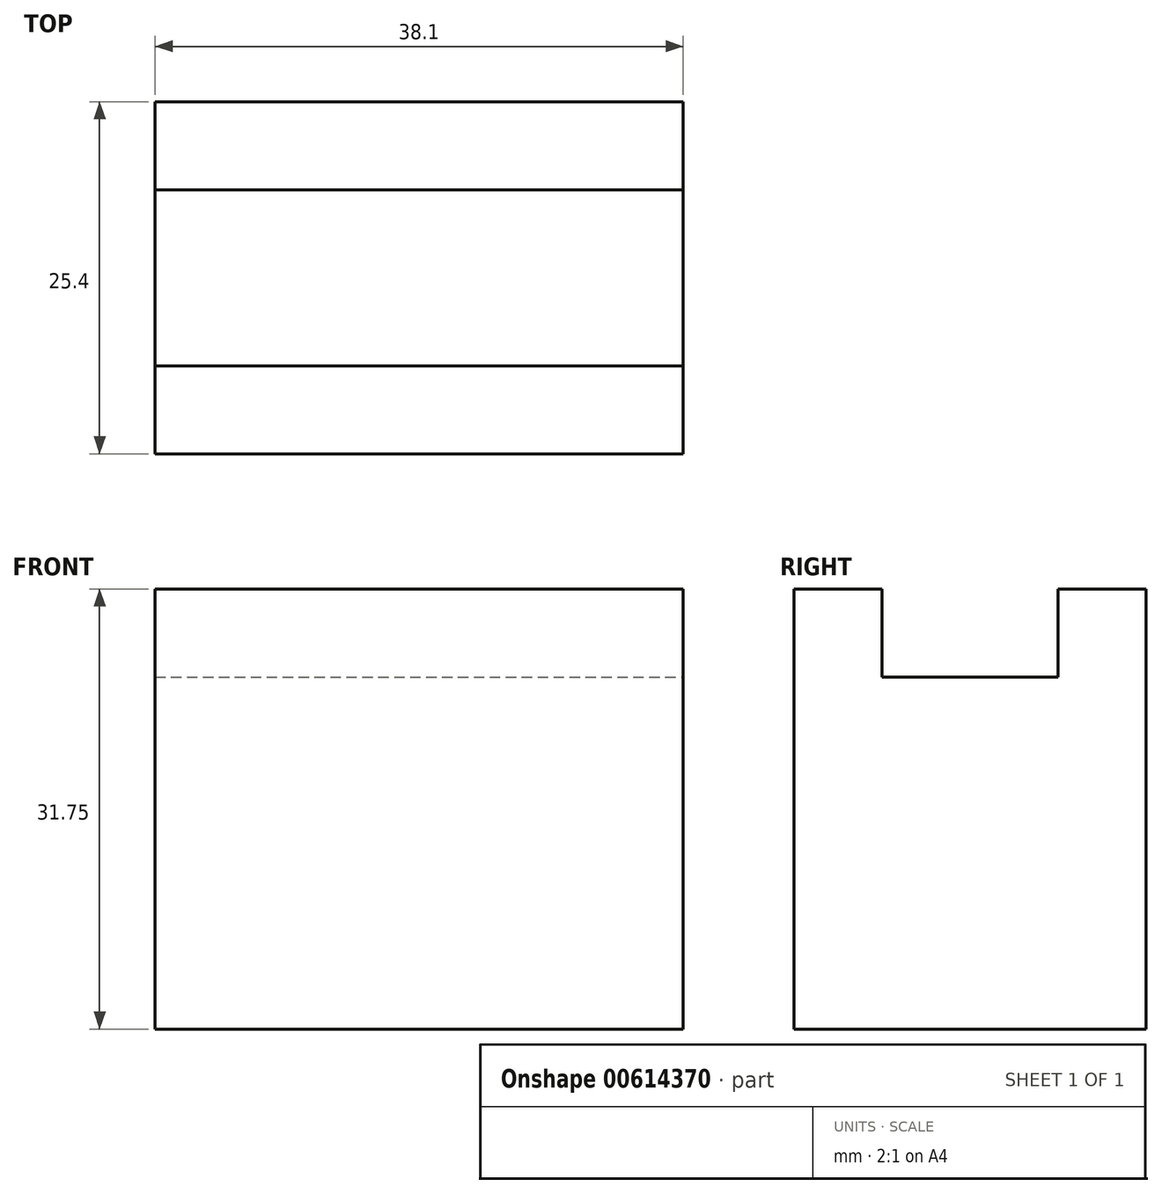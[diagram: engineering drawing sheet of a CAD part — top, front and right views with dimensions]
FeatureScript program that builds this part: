
annotation { "Feature Type Name" : "Feature", "Feature Type Description" : "" }
export const myFeature = defineFeature(function(context is Context, id is Id, definition is map)
    precondition{}
    {
        {
            var Q0;
            Q0=qCreatedBy(makeId("Front.planeOp"),FACE);
            var sketch = newSketch(context, id + "F0", { "sketchPlane" : qUnion([Q0])});
            skLineSegment(sketch, "E0", {"start": v(0, 0) * mm, "end": v(38.1, 0) * mm});
            skLineSegment(sketch, "E1", {"start": v(38.1, 0) * mm, "end": v(38.1, 31.75) * mm});
            skLineSegment(sketch, "E2", {"start": v(0, 0) * mm, "end": v(0, 31.75) * mm});
            skLineSegment(sketch, "E3", {"start": v(0, 31.75) * mm, "end": v(38.1, 31.75) * mm});
            skSolve(sketch);
        }
        {
            var Q0;
            Q0 = qSketchRegion(id + "F0", true);
            extrude(context, id + "F1", {"entities" : qUnion([Q0]), "depth" : 25.4 * mm, "offsetDistance" : 25.4 * mm});
        }
        {
            var Q0;
            Q0=makeQuery(id+"F1.opExtrude","SWEPT_FACE",FACE,{"disambiguationData":[OSD([sQuery(id+"F0.wireOp",EDGE,"E3")])]});
            var sketch = newSketch(context, id + "F2", { "sketchPlane" : qUnion([Q0])});
            skLineSegment(sketch, "E4", {"start": v(0, 0) * mm, "end": v(0, -6.35) * mm});
            skLineSegment(sketch, "E5", {"start": v(0, -25.4) * mm, "end": v(0, -19.05) * mm});
            skLineSegment(sketch, "E6", {"start": v(0, -19.05) * mm, "end": v(38.1, -19.05) * mm});
            skLineSegment(sketch, "E7", {"start": v(0, -6.35) * mm, "end": v(38.1, -6.35) * mm});
            skLineSegment(sketch, "E8", {"start": v(0, -6.35) * mm, "end": v(0, -19.05) * mm});
            skLineSegment(sketch, "E9", {"start": v(38.1, -6.35) * mm, "end": v(38.1, -19.05) * mm});
            skSolve(sketch);
        }
        {
            var Q0;
            Q0=makeQuery(id+"F2.imprint","IMPRINT",FACE,{"disambiguationData":[TD([[makeQuery(id+"F2.imprint","IMPRINT",EDGE,{"derivedFrom":sQuery(id+"F2.wireOp",EDGE,"E6")}),1.0]])]});
            var Q1;
            Q1=makeQuery(id+"F1.opExtrude","SWEPT_FACE",FACE,{"disambiguationData":[OSD([sQuery(id+"F0.wireOp",EDGE,"E0")])]});
            extrude(context, id + "F3", {"entities" : qUnion([Q0, Q1]), "operationType" : NewBodyOperationType.REMOVE, "oppositeDirection" : true, "depth" : 6.35 * mm, "offsetDistance" : 25.4 * mm});
        }
        {
            var Q0;
            Q0=makeQuery(id+"F1.opExtrude","SWEPT_FACE",FACE,{"disambiguationData":[OSD([sQuery(id+"F0.wireOp",EDGE,"E0")])]});
            var sketch = newSketch(context, id + "F4", { "sketchPlane" : qUnion([Q0])});
            skLineSegment(sketch, "E10", {"start": v(0, 25.4) * mm, "end": v(12.7, 25.4) * mm});
            skLineSegment(sketch, "E11", {"start": v(38.1, 25.4) * mm, "end": v(25.4, 25.4) * mm});
            skLineSegment(sketch, "E12", {"start": v(12.7, 25.4) * mm, "end": v(12.7, 0) * mm});
            skLineSegment(sketch, "E13", {"start": v(25.4, 25.4) * mm, "end": v(25.4, 0) * mm});
            skLineSegment(sketch, "E14", {"start": v(12.7, 25.4) * mm, "end": v(25.4, 25.4) * mm});
            skLineSegment(sketch, "E15", {"start": v(12.7, 0) * mm, "end": v(25.4, 0) * mm});
            skSolve(sketch);
        }
        {
            var Q0;
            Q0 = qSketchRegion(id + "F4", true);
            extrude(context, id + "F5", {"entities" : qUnion([Q0]), "operationType" : NewBodyOperationType.ADD, "depth" : 6.35 * mm, "offsetDistance" : 25.4 * mm});
        }
        {
            var Q0;
            Q0=makeQuery(id+"F5.opExtrude","CAP_FACE",FACE,{"disambiguationData":[OSD([sQuery(id+"F4.wireOp",EDGE,"E12"),sQuery(id+"F4.wireOp",EDGE,"E13"),sQuery(id+"F4.wireOp",EDGE,"E14"),sQuery(id+"F4.wireOp",EDGE,"E15")])],"isStart":false});
            extrude(context, id + "F6", {"entities" : qUnion([Q0]), "operationType" : NewBodyOperationType.ADD, "depth" : 25.4 * mm, "offsetDistance" : 25.4 * mm});
        }
        {
            var Q0;
            {var subQ0=sQuery(id+"F4.wireOp",EDGE,"E13");Q0=makeQuery(id+"F6.boolean.opBoolean","MERGE",FACE,{"derivedFrom":[makeQuery(id+"F5.opExtrude","SWEPT_FACE",FACE,{"disambiguationData":[OSD([subQ0])]}),makeQuery(id+"F6.opExtrude","SWEPT_FACE",FACE,{"disambiguationData":[OSD([subQ0])]})]});}
            extrude(context, id + "F7", {"entities" : qUnion([Q0]), "operationType" : NewBodyOperationType.REMOVE, "oppositeDirection" : true, "depth" : 12.7 * mm, "offsetDistance" : 25.4 * mm});
        }
    });
